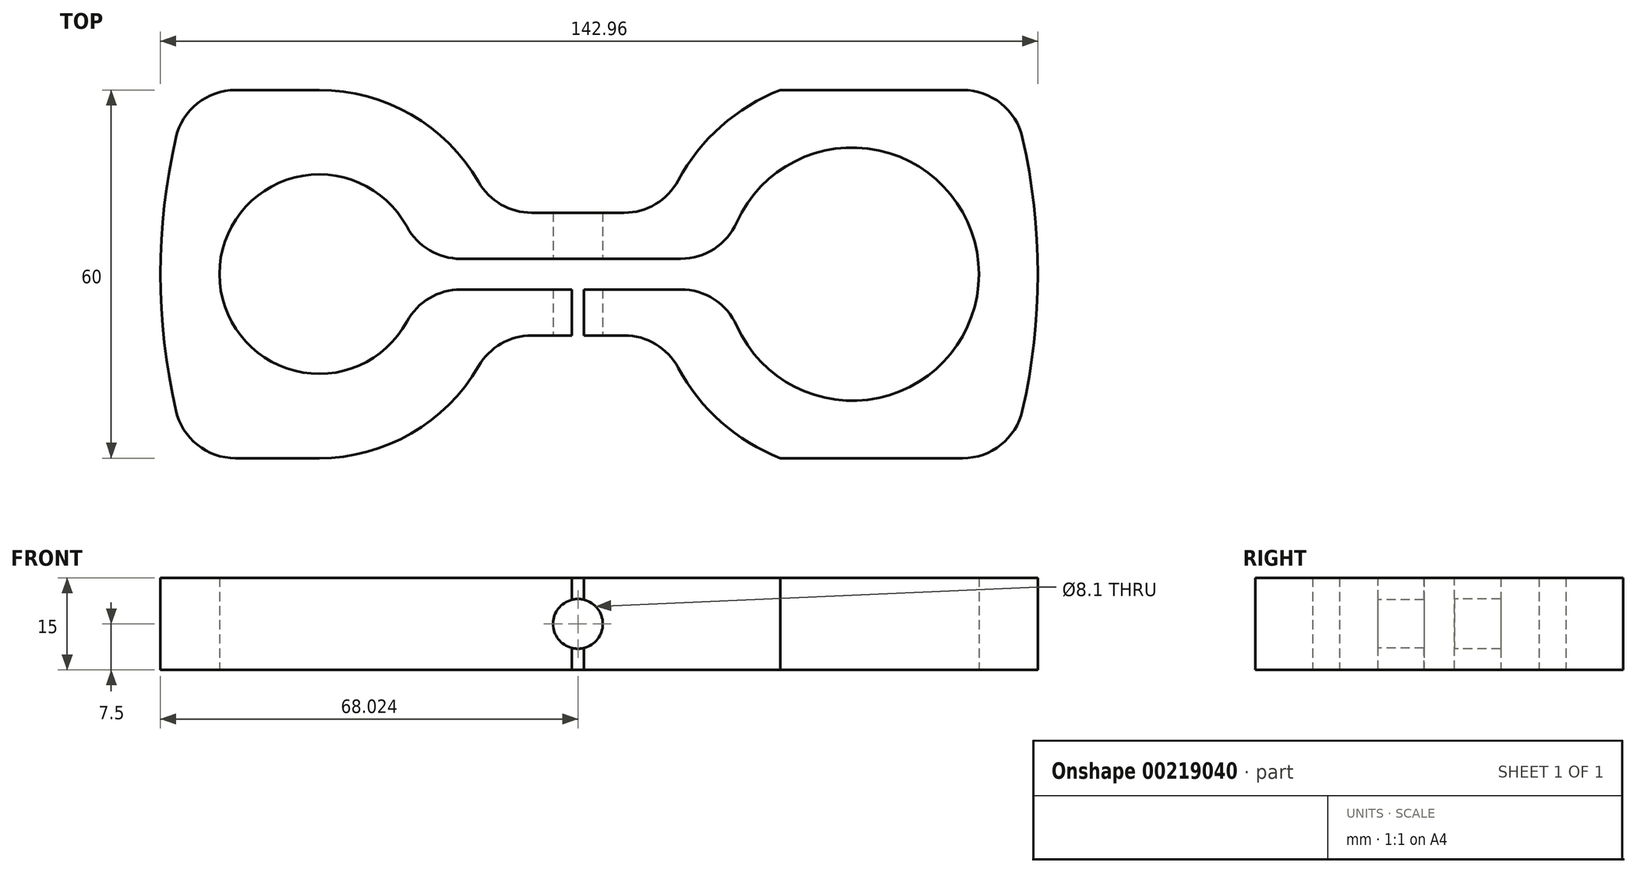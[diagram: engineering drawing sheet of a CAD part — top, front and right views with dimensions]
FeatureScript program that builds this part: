
annotation { "Feature Type Name" : "Feature", "Feature Type Description" : "" }
export const myFeature = defineFeature(function(context is Context, id is Id, definition is map)
    precondition{}
    {
        {
            var Q0;
            Q0=qCreatedBy(makeId("Top.planeOp"),FACE);
            var sketch = newSketch(context, id + "F0", { "sketchPlane" : qUnion([Q0])});
            skCircle(sketch, "E0", {"center": v(0, 0) * mm, "radius": 20.62 * mm});
            skCircle(sketch, "E1", {"center": v(-86.88, 0) * mm, "radius": 16.25 * mm});
            skLineSegment(sketch, "E2.bottom", {"start": v(25.62, 30) * mm, "end": v(-11.74, 30) * mm});
            skLineSegment(sketch, "E2.top", {"start": v(25.63, -30) * mm, "end": v(-11.74, -30) * mm});
            skLineSegment(sketch, "E2.left", {"start": v(25.62, 30) * mm, "end": v(25.63, -30) * mm});
            skLineSegment(sketch, "E2.right", {"start": v(-108.13, 30) * mm, "end": v(-108.13, -30) * mm});
            skLineSegment(sketch, "E3.top", {"start": v(-58.6, 10) * mm, "end": v(-30.63, 10) * mm});
            skLineSegment(sketch, "E4.top", {"start": v(-60.63, -10) * mm, "end": v(-30.62, -10) * mm});
            skLineSegment(sketch, "E4.left", {"start": v(-60.62, -14.52) * mm, "end": v(-60.63, -10) * mm});
            skArc(sketch, "E5", {"start": v(-30.62, 10) * mm, "mid": v(-23.43, 22.12) * mm, "end": v(-11.74, 30) * mm});
            skArc(sketch, "E6", {"start": v(-86.88, 30) * mm, "mid": v(-69.55, 24.5) * mm, "end": v(-58.6, 10) * mm});
            skArc(sketch, "E7", {"start": v(-86.88, -30) * mm, "mid": v(-71.64, -25.84) * mm, "end": v(-60.62, -14.52) * mm});
            skLineSegment(sketch, "E8.trimOffspring", {"start": v(-86.88, -30) * mm, "end": v(-108.13, -30) * mm});
            skLineSegment(sketch, "E9.trimOffspring", {"start": v(-86.88, 30) * mm, "end": v(-108.13, 30) * mm});
            skArc(sketch, "E10", {"start": v(-30.62, -10) * mm, "mid": v(-23.43, -22.12) * mm, "end": v(-11.74, -30) * mm});
            skLineSegment(sketch, "E11.bottom", {"start": v(-70.82, 2.5) * mm, "end": v(-20.47, 2.5) * mm});
            skLineSegment(sketch, "E11.top", {"start": v(-70.82, -2.5) * mm, "end": v(-20.47, -2.5) * mm});
            skLineSegment(sketch, "E11.left", {"start": v(-70.82, 2.5) * mm, "end": v(-70.82, -2.5) * mm});
            skLineSegment(sketch, "E11.right", {"start": v(-20.47, 2.5) * mm, "end": v(-20.47, -2.5) * mm});
            skArc(sketch, "E12", {"start": v(-108.12, 30) * mm, "mid": v(-112.73, 0) * mm, "end": v(-108.12, -30) * mm});
            skArc(sketch, "E13", {"start": v(25.62, -30) * mm, "mid": v(30.23, 0) * mm, "end": v(25.62, 30) * mm});
            skArc(sketch, "E14", {"start": v(-86.88, -30) * mm, "mid": v(-69.55, -24.5) * mm, "end": v(-58.6, -10) * mm});
            skSolve(sketch);
        }
        {
            var Q0;
            Q0 = qSketchRegion(id + "F0", true);
            extrude(context, id + "F1", {"entities" : qUnion([Q0]), "depth" : 15 * mm});
        }
        {
            var Q0;
            Q0=makeQuery(id+"F1.opExtrude","SWEPT_EDGE",EDGE,{"disambiguationData":[OSD([sQuery(id+"F0.wireOp",EDGE,"E2.right"),sQuery(id+"F0.wireOp",EDGE,"E8.trimOffspring"),sQuery(id+"F0.wireOp",EDGE,"E12")])]});
            var Q1;
            Q1=makeQuery(id+"F1.opExtrude","SWEPT_EDGE",EDGE,{"disambiguationData":[OSD([sQuery(id+"F0.wireOp",EDGE,"E2.right"),sQuery(id+"F0.wireOp",EDGE,"E9.trimOffspring"),sQuery(id+"F0.wireOp",EDGE,"E12")])]});
            var Q2;
            Q2=makeQuery(id+"F1.opExtrude","SWEPT_EDGE",EDGE,{"disambiguationData":[OSD([sQuery(id+"F0.wireOp",EDGE,"E2.bottom"),sQuery(id+"F0.wireOp",EDGE,"E2.left"),sQuery(id+"F0.wireOp",EDGE,"E13")])]});
            var Q3;
            Q3=makeQuery(id+"F1.opExtrude","SWEPT_EDGE",EDGE,{"disambiguationData":[OSD([sQuery(id+"F0.wireOp",EDGE,"E2.top"),sQuery(id+"F0.wireOp",EDGE,"E2.left"),sQuery(id+"F0.wireOp",EDGE,"E13")])]});
            var Q4;
            Q4=makeQuery(id+"F1.opExtrude","SWEPT_EDGE",EDGE,{"disambiguationData":[OSD([sQuery(id+"F0.wireOp",EDGE,"E0"),sQuery(id+"F0.wireOp",EDGE,"E11.top"),sQuery(id+"F0.wireOp",EDGE,"E11.right")])]});
            var Q5;
            Q5=makeQuery(id+"F1.opExtrude","SWEPT_EDGE",EDGE,{"disambiguationData":[OSD([sQuery(id+"F0.wireOp",EDGE,"E0"),sQuery(id+"F0.wireOp",EDGE,"E11.bottom"),sQuery(id+"F0.wireOp",EDGE,"E11.right")])]});
            var Q6;
            Q6=makeQuery(id+"F1.opExtrude","SWEPT_EDGE",EDGE,{"disambiguationData":[OSD([sQuery(id+"F0.wireOp",EDGE,"E1"),sQuery(id+"F0.wireOp",EDGE,"E11.bottom"),sQuery(id+"F0.wireOp",EDGE,"E11.left")])]});
            var Q7;
            Q7=makeQuery(id+"F1.opExtrude","SWEPT_EDGE",EDGE,{"disambiguationData":[OSD([sQuery(id+"F0.wireOp",EDGE,"E1"),sQuery(id+"F0.wireOp",EDGE,"E11.top"),sQuery(id+"F0.wireOp",EDGE,"E11.left")])]});
            var Q8;
            Q8=makeQuery(id+"F1.opExtrude","SWEPT_EDGE",EDGE,{"disambiguationData":[OSD([sQuery(id+"F0.wireOp",EDGE,"E4.top"),sQuery(id+"F0.wireOp",EDGE,"E14")])]});
            var Q9;
            Q9=makeQuery(id+"F1.opExtrude","SWEPT_EDGE",EDGE,{"disambiguationData":[OSD([sQuery(id+"F0.wireOp",EDGE,"E4.top"),sQuery(id+"F0.wireOp",EDGE,"E10")])]});
            var Q10;
            Q10=makeQuery(id+"F1.opExtrude","SWEPT_EDGE",EDGE,{"disambiguationData":[OSD([sQuery(id+"F0.wireOp",EDGE,"E3.top"),sQuery(id+"F0.wireOp",EDGE,"E5")])]});
            var Q11;
            Q11=makeQuery(id+"F1.opExtrude","SWEPT_EDGE",EDGE,{"disambiguationData":[OSD([sQuery(id+"F0.wireOp",EDGE,"E3.top"),sQuery(id+"F0.wireOp",EDGE,"E6")])]});
            fillet(context, id + "F2", {"entities" : qUnion([Q0, Q1, Q2, Q3, Q4, Q5, Q6, Q7, Q8, Q9, Q10, Q11]), "radius" : 10 * mm, "tangentPropagation" : true, "allowEdgeOverflow" : false});
        }
        {
            var Q0;
            Q0=makeQuery(id+"F1.opExtrude","SWEPT_FACE",FACE,{"disambiguationData":[OSD([sQuery(id+"F0.wireOp",EDGE,"E4.top")])]});
            var sketch = newSketch(context, id + "F3", { "sketchPlane" : qUnion([Q0])});
            skLineSegment(sketch, "E15", {"start": v(-52.23, 15) * mm, "end": v(-37.18, 0) * mm, "construction": true});
            skPoint(sketch, "E16", {"position": v(-44.7, 7.5) * mm});
            skSolve(sketch);
        }
        {
            var Q0;
            Q0=sQuery(id+"F3.wireOp",VERTEX,"E16");
            var Q1;
            Q1=makeQuery(id+"F1.opExtrude","SWEPT_BODY",BODY,{"disambiguationData":[OSD([sQuery(id+"F0.wireOp",EDGE,"E0"),sQuery(id+"F0.wireOp",EDGE,"E1"),sQuery(id+"F0.wireOp",EDGE,"E2.bottom"),sQuery(id+"F0.wireOp",EDGE,"E2.top"),sQuery(id+"F0.wireOp",EDGE,"E3.top"),sQuery(id+"F0.wireOp",EDGE,"E4.top"),sQuery(id+"F0.wireOp",EDGE,"E5"),sQuery(id+"F0.wireOp",EDGE,"E6"),sQuery(id+"F0.wireOp",EDGE,"E8.trimOffspring"),sQuery(id+"F0.wireOp",EDGE,"E9.trimOffspring"),sQuery(id+"F0.wireOp",EDGE,"E10"),sQuery(id+"F0.wireOp",EDGE,"E11.bottom"),sQuery(id+"F0.wireOp",EDGE,"E11.top"),sQuery(id+"F0.wireOp",EDGE,"E12"),sQuery(id+"F0.wireOp",EDGE,"E13"),sQuery(id+"F0.wireOp",EDGE,"E14")])]});
            hole(context, id + "F4", {"style" : HoleStyle.SIMPLE, "endStyle" : HoleEndStyle.THROUGH, "holeDiameter" : 8.1 * mm, "startFromSketch" : true, "locations" : qUnion([Q0]), "scope" : qUnion([Q1]), "isTappedThrough" : true});
        }
        {
            var Q0;
            Q0=makeQuery(id+"F1.opExtrude","CAP_FACE",FACE,{"disambiguationData":[OSD([sQuery(id+"F0.wireOp",EDGE,"E0"),sQuery(id+"F0.wireOp",EDGE,"E1"),sQuery(id+"F0.wireOp",EDGE,"E2.bottom"),sQuery(id+"F0.wireOp",EDGE,"E2.top"),sQuery(id+"F0.wireOp",EDGE,"E3.top"),sQuery(id+"F0.wireOp",EDGE,"E4.top"),sQuery(id+"F0.wireOp",EDGE,"E5"),sQuery(id+"F0.wireOp",EDGE,"E6"),sQuery(id+"F0.wireOp",EDGE,"E8.trimOffspring"),sQuery(id+"F0.wireOp",EDGE,"E9.trimOffspring"),sQuery(id+"F0.wireOp",EDGE,"E10"),sQuery(id+"F0.wireOp",EDGE,"E11.bottom"),sQuery(id+"F0.wireOp",EDGE,"E11.top"),sQuery(id+"F0.wireOp",EDGE,"E12"),sQuery(id+"F0.wireOp",EDGE,"E13"),sQuery(id+"F0.wireOp",EDGE,"E14")])],"isStart":false});
            var sketch = newSketch(context, id + "F5", { "sketchPlane" : qUnion([Q0])});
            skLineSegment(sketch, "E17.0", {"start": v(-40.66, -10) * mm, "end": v(-48.76, -10) * mm, "construction": true});
            skPoint(sketch, "E18", {"position": v(-44.7, -10) * mm});
            skLineSegment(sketch, "E19.bottom", {"start": v(-45.7, -10) * mm, "end": v(-43.7, -10) * mm});
            skLineSegment(sketch, "E19.top", {"start": v(-45.7, -2.5) * mm, "end": v(-43.7, -2.5) * mm});
            skLineSegment(sketch, "E19.left", {"start": v(-45.7, -10) * mm, "end": v(-45.7, -2.5) * mm});
            skLineSegment(sketch, "E19.right", {"start": v(-43.7, -10) * mm, "end": v(-43.7, -2.5) * mm});
            skSolve(sketch);
        }
        {
            var Q0;
            Q0=makeQuery(id+"F5.imprint","IMPRINT",FACE,{"disambiguationData":[TD([[makeQuery(id+"F5.imprint","IMPRINT",EDGE,{"derivedFrom":sQuery(id+"F5.wireOp",EDGE,"E19.bottom")}),1.0]])]});
            extrude(context, id + "F6", {"entities" : qUnion([Q0]), "operationType" : NewBodyOperationType.REMOVE, "endBound" : BoundingType.THROUGH_ALL, "oppositeDirection" : true, "depth" : 25 * mm});
        }
    });
